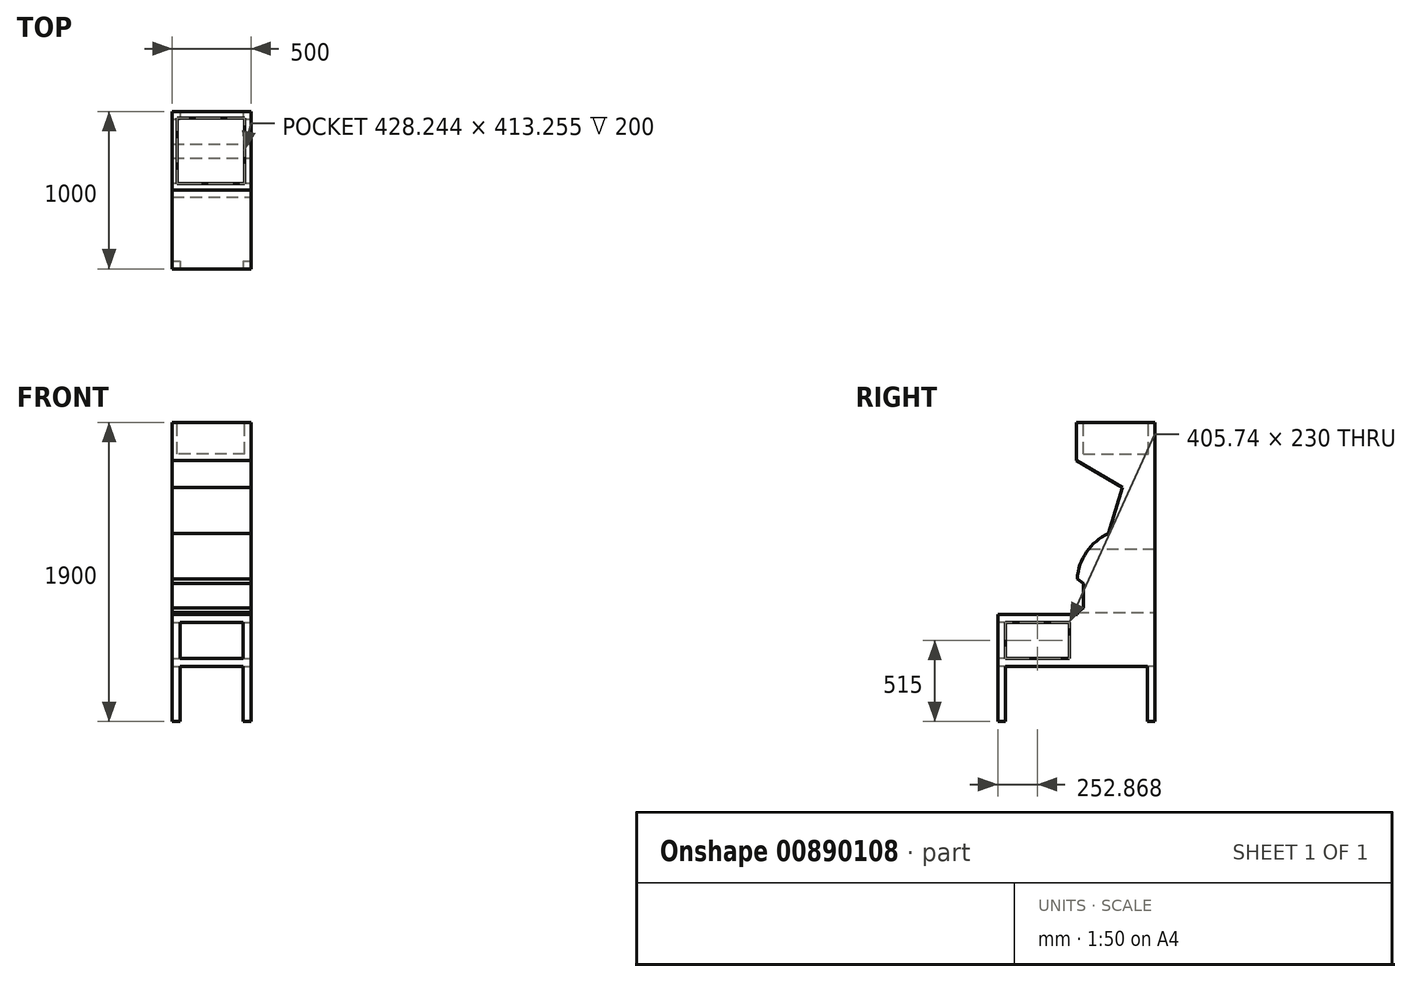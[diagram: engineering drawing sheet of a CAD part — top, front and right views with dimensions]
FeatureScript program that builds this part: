
annotation { "Feature Type Name" : "Feature", "Feature Type Description" : "" }
export const myFeature = defineFeature(function(context is Context, id is Id, definition is map)
    precondition{}
    {
        {
            var Q0;
            Q0=qCreatedBy(makeId("Top.planeOp"),FACE);
            var sketch = newSketch(context, id + "F0", { "sketchPlane" : qUnion([Q0])});
            skLineSegment(sketch, "E0", {"start": v(0, 0) * mm, "end": v(0, 1000) * mm});
            skLineSegment(sketch, "E1", {"start": v(0, 1000) * mm, "end": v(-500, 1000) * mm});
            skLineSegment(sketch, "E2", {"start": v(-500, 1000) * mm, "end": v(-500, 0) * mm});
            skLineSegment(sketch, "E3", {"start": v(-500, 0) * mm, "end": v(0, 0) * mm});
            skSolve(sketch);
        }
        {
            var Q0;
            Q0=makeQuery(id+"F0.imprint","IMPRINT",FACE,{"disambiguationData":[TD([[makeQuery(id+"F0.imprint","IMPRINT",EDGE,{"derivedFrom":sQuery(id+"F0.wireOp",EDGE,"E0")}),1.0]])]});
            extrude(context, id + "F1", {"entities" : qUnion([Q0]), "depth" : 1900 * mm, "offsetDistance" : 25 * mm});
        }
        {
            var Q0;
            Q0=makeQuery(id+"F1.opExtrude","SWEPT_FACE",FACE,{"disambiguationData":[OSD([sQuery(id+"F0.wireOp",EDGE,"E0")])]});
            var sketch = newSketch(context, id + "F2", { "sketchPlane" : qUnion([Q0])});
            skLineSegment(sketch, "E4", {"start": v(0, 0) * mm, "end": v(50, 0) * mm});
            skLineSegment(sketch, "E5", {"start": v(50, 0) * mm, "end": v(50, 350) * mm});
            skLineSegment(sketch, "E6", {"start": v(1000, 0) * mm, "end": v(950, 0) * mm});
            skLineSegment(sketch, "E7", {"start": v(950, 0) * mm, "end": v(950, 350) * mm});
            skLineSegment(sketch, "E8", {"start": v(950, 350) * mm, "end": v(50, 350) * mm});
            skSolve(sketch);
        }
        {
            var Q0;
            {var subQ0=sQuery(id+"F2.wireOp",EDGE,"E5");Q0=makeQuery(id+"F2.imprint","IMPRINT",FACE,{"disambiguationData":[TD([[makeQuery(id+"F2.imprint","IMPRINT",EDGE,{"derivedFrom":subQ0}),-1.0]])]});}
            extrude(context, id + "F3", {"entities" : qUnion([Q0]), "operationType" : NewBodyOperationType.REMOVE, "oppositeDirection" : true, "depth" : 500 * mm, "offsetDistance" : 25 * mm});
        }
        {
            var Q0;
            Q0=makeQuery(id+"F1.opExtrude","SWEPT_FACE",FACE,{"disambiguationData":[OSD([sQuery(id+"F0.wireOp",EDGE,"E3")])]});
            var sketch = newSketch(context, id + "F4", { "sketchPlane" : qUnion([Q0])});
            skLineSegment(sketch, "E9", {"start": v(-500, 0) * mm, "end": v(-450, 0) * mm});
            skLineSegment(sketch, "E10", {"start": v(-450, 0) * mm, "end": v(-450, 350) * mm});
            skLineSegment(sketch, "E11", {"start": v(0, 0) * mm, "end": v(-50, 0) * mm});
            skLineSegment(sketch, "E12", {"start": v(-50, 0) * mm, "end": v(-50, 350) * mm});
            skLineSegment(sketch, "E13", {"start": v(-50, 350) * mm, "end": v(-450, 350) * mm});
            skSolve(sketch);
        }
        {
            var Q0;
            {var subQ0=sQuery(id+"F4.wireOp",EDGE,"E10");Q0=makeQuery(id+"F4.imprint","IMPRINT",FACE,{"disambiguationData":[TD([[makeQuery(id+"F4.imprint","IMPRINT",EDGE,{"derivedFrom":subQ0}),-1.0]])]});}
            extrude(context, id + "F5", {"entities" : qUnion([Q0]), "operationType" : NewBodyOperationType.REMOVE, "oppositeDirection" : true, "depth" : 1000 * mm, "offsetDistance" : 25 * mm});
        }
        {
            var Q0;
            Q0=makeQuery(id+"F1.opExtrude","SWEPT_FACE",FACE,{"disambiguationData":[OSD([sQuery(id+"F0.wireOp",EDGE,"E0")])]});
            var sketch = newSketch(context, id + "F6", { "sketchPlane" : qUnion([Q0])});
            skLineSegment(sketch, "E14", {"start": v(1000, 1900) * mm, "end": v(500, 1900) * mm});
            skLineSegment(sketch, "E15", {"start": v(500, 1900) * mm, "end": v(500, 1657.03) * mm});
            skLineSegment(sketch, "E16", {"start": v(500, 1657.03) * mm, "end": v(792.62, 1488.1) * mm});
            skLineSegment(sketch, "E17", {"start": v(505.74, 905.25) * mm, "end": v(544.32, 876.87) * mm});
            skLineSegment(sketch, "E18", {"start": v(544.32, 876.87) * mm, "end": v(544.32, 722.31) * mm});
            skLineSegment(sketch, "E19", {"start": v(544.32, 722.31) * mm, "end": v(505.74, 692.8) * mm});
            skLineSegment(sketch, "E20", {"start": v(505.74, 692.8) * mm, "end": v(505.74, 350) * mm});
            skLineSegment(sketch, "E21", {"start": v(50, 350) * mm, "end": v(50, 400) * mm});
            skLineSegment(sketch, "E22", {"start": v(50, 400) * mm, "end": v(50, 630) * mm});
            skLineSegment(sketch, "E23", {"start": v(505.74, 350) * mm, "end": v(505.74, 400) * mm});
            skLineSegment(sketch, "E24", {"start": v(505.74, 400) * mm, "end": v(455.74, 400) * mm});
            skLineSegment(sketch, "E25", {"start": v(455.74, 400) * mm, "end": v(455.74, 630) * mm});
            skLineSegment(sketch, "E26", {"start": v(455.74, 630) * mm, "end": v(50, 630) * mm});
            skLineSegment(sketch, "E27", {"start": v(50, 400) * mm, "end": v(455.74, 400) * mm});
            skLineSegment(sketch, "E28", {"start": v(455.74, 680) * mm, "end": v(50, 680) * mm});
            skLineSegment(sketch, "E29", {"start": v(50, 680) * mm, "end": v(0, 680) * mm});
            skPoint(sketch, "E29.endSnap0", {"position": v(0, 950) * mm});
            skLineSegment(sketch, "E30", {"start": v(0, 680) * mm, "end": v(505.74, 680) * mm});
            skLineSegment(sketch, "E31", {"start": v(792.62, 1488.1) * mm, "end": v(703.89, 1194.45) * mm});
            skArc(sketch, "E32", {"start": v(703.89, 1194.45) * mm, "mid": v(564.79, 1077.27) * mm, "end": v(505.74, 905.25) * mm});
            skSolve(sketch);
        }
        {
            var Q0;
            Q0=makeQuery(id+"F6.imprint","IMPRINT",FACE,{"disambiguationData":[TD([[makeQuery(id+"F6.imprint","IMPRINT",EDGE,{"derivedFrom":sQuery(id+"F6.wireOp",EDGE,"E22")}),-1.0]])]});
            extrude(context, id + "F7", {"entities" : qUnion([Q0]), "operationType" : NewBodyOperationType.REMOVE, "oppositeDirection" : true, "depth" : 500 * mm, "offsetDistance" : 25 * mm});
        }
        {
            var Q0;
            {var subQ4=sQuery(id+"F6.wireOp",EDGE,"E15");Q0=makeQuery(id+"F6.imprint","IMPRINT",FACE,{"disambiguationData":[TD([[makeQuery(id+"F6.imprint","IMPRINT",EDGE,{"derivedFrom":subQ4}),-1.0]])]});}
            extrude(context, id + "F8", {"entities" : qUnion([Q0]), "operationType" : NewBodyOperationType.REMOVE, "oppositeDirection" : true, "depth" : 500 * mm, "offsetDistance" : 25 * mm});
        }
        {
            var Q0;
            Q0=makeQuery(id+"F1.opExtrude","CAP_FACE",FACE,{"disambiguationData":[OSD([sQuery(id+"F0.wireOp",EDGE,"E0"),sQuery(id+"F0.wireOp",EDGE,"E1"),sQuery(id+"F0.wireOp",EDGE,"E2"),sQuery(id+"F0.wireOp",EDGE,"E3")])],"isStart":false});
            var sketch = newSketch(context, id + "F9", { "sketchPlane" : qUnion([Q0])});
            skLineSegment(sketch, "E33.bottom", {"start": v(-39.1, 543.37) * mm, "end": v(-467.33, 543.37) * mm});
            skLineSegment(sketch, "E33.top", {"start": v(-39.1, 956.63) * mm, "end": v(-467.33, 956.63) * mm});
            skLineSegment(sketch, "E33.left", {"start": v(-39.1, 543.37) * mm, "end": v(-39.1, 956.63) * mm});
            skLineSegment(sketch, "E33.right", {"start": v(-467.33, 543.37) * mm, "end": v(-467.33, 956.63) * mm});
            skPoint(sketch, "E33.middle", {"position": v(-253.21, 750) * mm});
            skPoint(sketch, "E33.middle.positionSnap0", {"position": v(0, 750) * mm});
            skPoint(sketch, "E33.centerSnap0", {"position": v(0, 750) * mm});
            skSolve(sketch);
        }
        {
            var Q0;
            Q0=makeQuery(id+"F9.imprint","IMPRINT",FACE,{"disambiguationData":[TD([[makeQuery(id+"F9.imprint","IMPRINT",EDGE,{"derivedFrom":sQuery(id+"F9.wireOp",EDGE,"E33.bottom")}),-1.0]])]});
            extrude(context, id + "F10", {"entities" : qUnion([Q0]), "operationType" : NewBodyOperationType.REMOVE, "oppositeDirection" : true, "depth" : 200 * mm, "offsetDistance" : 25 * mm});
        }
        {
            var Q0;
            Q0=makeQuery(id+"F1.opExtrude","SWEPT_FACE",FACE,{"disambiguationData":[OSD([sQuery(id+"F0.wireOp",EDGE,"E1")])]});
            var sketch = newSketch(context, id + "F11", { "sketchPlane" : qUnion([Q0])});
            skLineSegment(sketch, "E34", {"start": v(500, 692.87) * mm, "end": v(414.23, 692.87) * mm});
            skLineSegment(sketch, "E35", {"start": v(414.23, 692.87) * mm, "end": v(414.23, 1094.74) * mm});
            skLineSegment(sketch, "E36", {"start": v(414.23, 1094.74) * mm, "end": v(500, 1094.74) * mm});
            skSolve(sketch);
        }
        {
            var Q0;
            {var subQ0=sQuery(id+"F11.wireOp",EDGE,"E34");Q0=makeQuery(id+"F11.imprint","IMPRINT",FACE,{"disambiguationData":[TD([[makeQuery(id+"F11.imprint","IMPRINT",EDGE,{"derivedFrom":subQ0}),-1.0]])]});}
            extrude(context, id + "F12", {"entities" : qUnion([Q0]), "operationType" : NewBodyOperationType.REMOVE, "oppositeDirection" : true, "depth" : 500 * mm, "offsetDistance" : 25 * mm});
        }
        {
            var Q0;
            Q0=makeQuery(id+"F1.opExtrude","SWEPT_FACE",FACE,{"disambiguationData":[OSD([sQuery(id+"F0.wireOp",EDGE,"E3")])]});
            var sketch = newSketch(context, id + "F13", { "sketchPlane" : qUnion([Q0])});
            skLineSegment(sketch, "E37", {"start": v(-450, 350) * mm, "end": v(-450, 400) * mm});
            skLineSegment(sketch, "E38", {"start": v(-50, 350) * mm, "end": v(-50, 400) * mm});
            skLineSegment(sketch, "E39", {"start": v(-50, 400) * mm, "end": v(-450, 400) * mm});
            skLineSegment(sketch, "E40", {"start": v(-500, 680) * mm, "end": v(-450, 680) * mm});
            skLineSegment(sketch, "E41", {"start": v(-450, 680) * mm, "end": v(-450, 630) * mm});
            skLineSegment(sketch, "E42", {"start": v(-450, 630) * mm, "end": v(-450, 400) * mm});
            skLineSegment(sketch, "E43", {"start": v(0, 680) * mm, "end": v(-50, 680) * mm});
            skLineSegment(sketch, "E44", {"start": v(-50, 680) * mm, "end": v(-50, 630) * mm});
            skLineSegment(sketch, "E45", {"start": v(-50, 630) * mm, "end": v(-50, 400) * mm});
            skLineSegment(sketch, "E46", {"start": v(-50, 630) * mm, "end": v(-450, 630) * mm});
            skSolve(sketch);
        }
        {
            var Q0;
            Q0=makeQuery(id+"F13.imprint","IMPRINT",FACE,{"disambiguationData":[TD([[makeQuery(id+"F13.imprint","IMPRINT",EDGE,{"derivedFrom":sQuery(id+"F13.wireOp",EDGE,"E39")}),-1.0]])]});
            extrude(context, id + "F14", {"entities" : qUnion([Q0]), "operationType" : NewBodyOperationType.REMOVE, "oppositeDirection" : true, "depth" : 50 * mm, "offsetDistance" : 25 * mm});
        }
        {
            var Q0;
            Q0=makeQuery(id+"F12.boolean.opBoolean","COPY",FACE,{"derivedFrom":makeQuery(id+"F12.opExtrude","SWEPT_FACE",FACE,{"disambiguationData":[OSD([sQuery(id+"F11.wireOp",EDGE,"E35")])]})});
            extrude(context, id + "F15", {"entities" : qUnion([Q0]), "operationType" : NewBodyOperationType.ADD, "depth" : 85 * mm, "offsetDistance" : 25 * mm});
        }
    });
